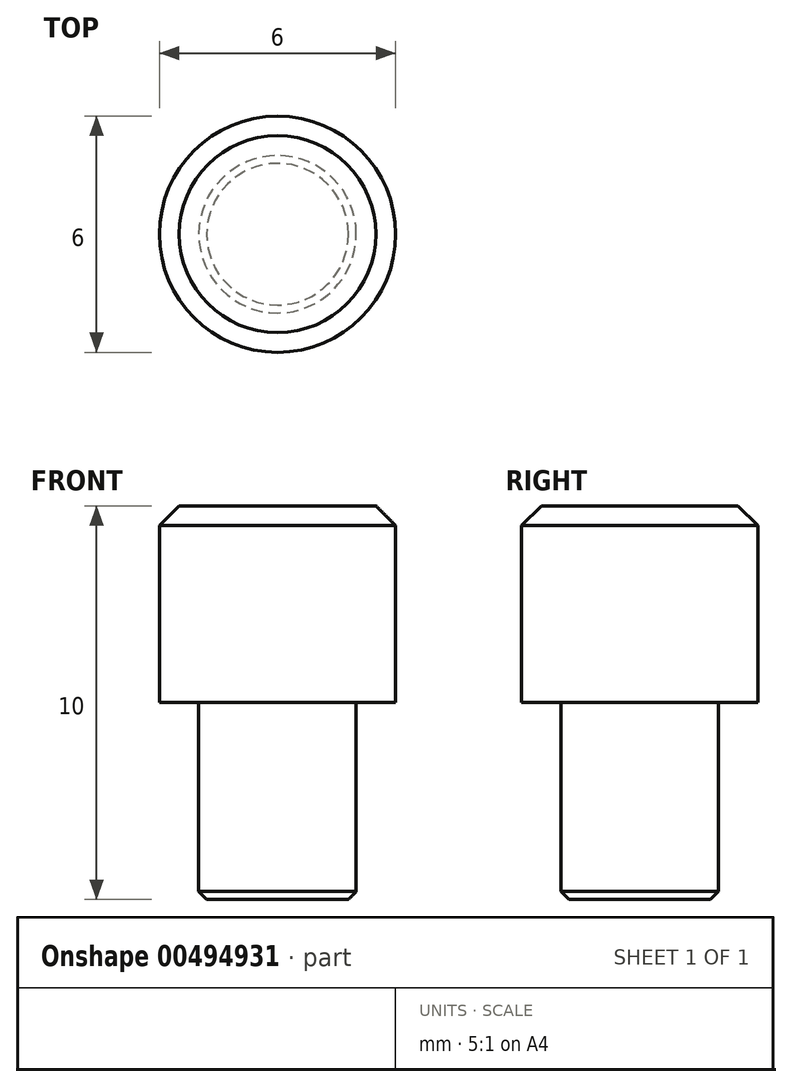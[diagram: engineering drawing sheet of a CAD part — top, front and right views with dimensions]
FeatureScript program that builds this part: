
annotation { "Feature Type Name" : "Feature", "Feature Type Description" : "" }
export const myFeature = defineFeature(function(context is Context, id is Id, definition is map)
    precondition{}
    {
        {
            var Q0;
            Q0=qCreatedBy(makeId("Top.planeOp"),FACE);
            var sketch = newSketch(context, id + "F0", { "sketchPlane" : qUnion([Q0])});
            skCircle(sketch, "E0", {"center": v(0, 0) * mm, "radius": 3 * mm});
            skSolve(sketch);
        }
        {
            var Q0;
            Q0=qSketchRegion(id+"F0",true);
            extrude(context, id + "F1", {"entities" : qUnion([Q0]), "depth" : 5 * mm});
        }
        {
            var Q0;
            Q0=qCreatedBy(makeId("Top.planeOp"),FACE);
            var sketch = newSketch(context, id + "F2", { "sketchPlane" : qUnion([Q0])});
            skCircle(sketch, "E1", {"center": v(0, 0) * mm, "radius": 2 * mm});
            skSolve(sketch);
        }
        {
            var Q0;
            Q0=qSketchRegion(id+"F2",true);
            extrude(context, id + "F3", {"entities" : qUnion([Q0]), "operationType" : NewBodyOperationType.ADD, "oppositeDirection" : true, "depth" : 5 * mm});
        }
        {
            var Q0;
            Q0=makeQuery(id+"F1.opExtrude","CAP_EDGE",EDGE,{"disambiguationData":[OSD([sQuery(id+"F0.wireOp",EDGE,"E0")])],"isStart":false});
            chamfer(context, id + "F4", {"entities" : qUnion([Q0]), "width" : 0.5 * mm, "tangentPropagation" : true});
        }
        {
            var Q0;
            Q0=makeQuery(id+"F3.opExtrude","CAP_EDGE",EDGE,{"disambiguationData":[OSD([sQuery(id+"F2.wireOp",EDGE,"E1")])],"isStart":false});
            chamfer(context, id + "F5", {"entities" : qUnion([Q0]), "width" : 0.2 * mm, "tangentPropagation" : true});
        }
    });
